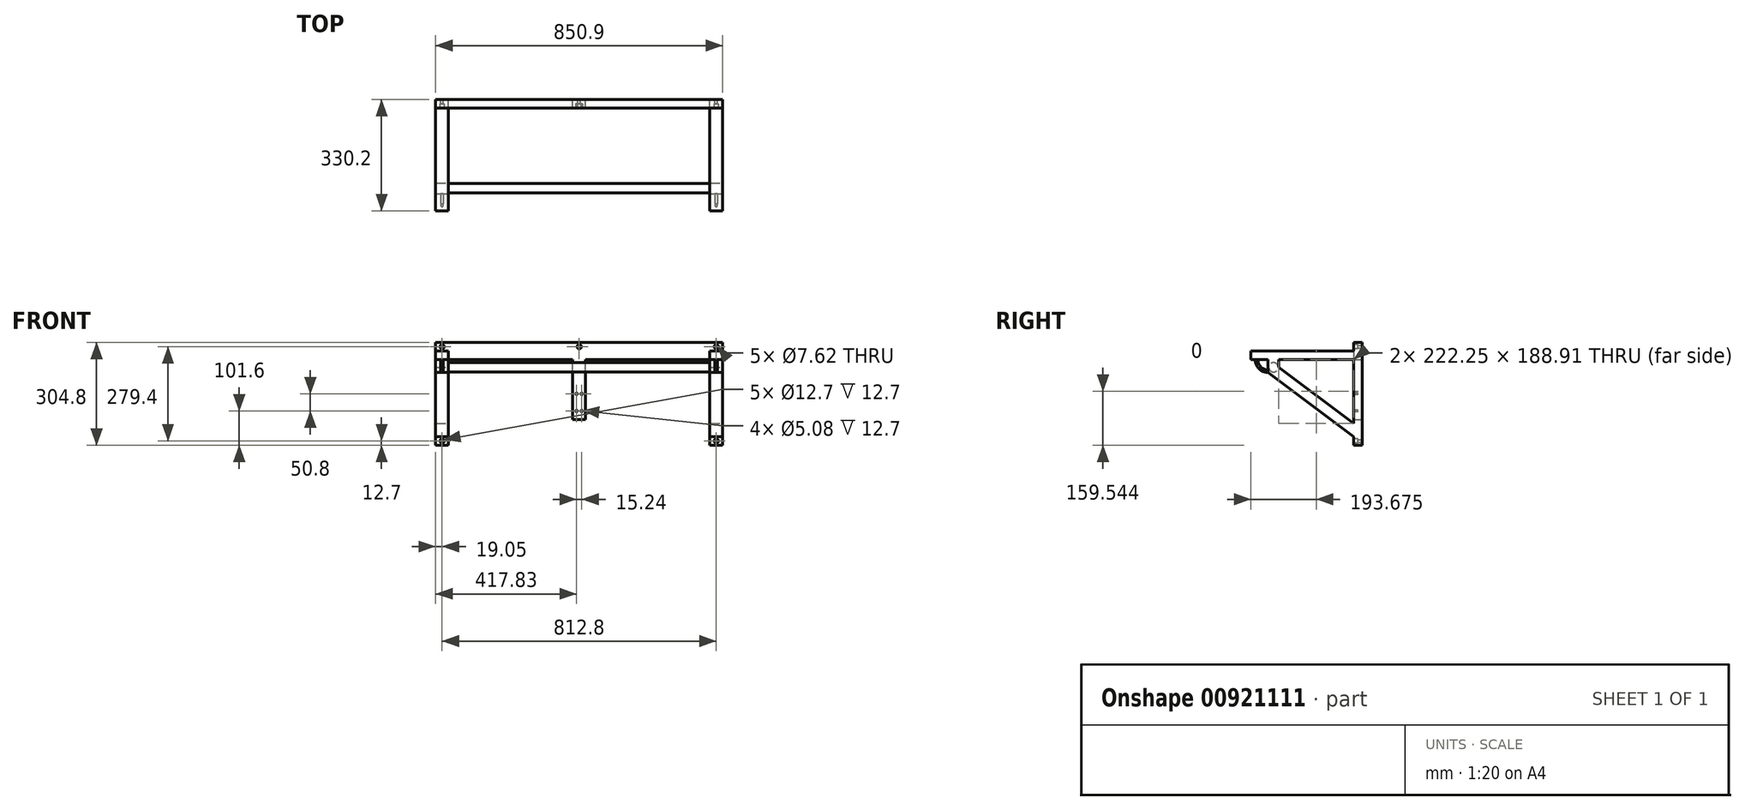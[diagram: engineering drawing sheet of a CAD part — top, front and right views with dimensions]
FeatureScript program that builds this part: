
annotation { "Feature Type Name" : "Feature", "Feature Type Description" : "" }
export const myFeature = defineFeature(function(context is Context, id is Id, definition is map)
    precondition{}
    {
        {
            var Q0;
            Q0=qCreatedBy(makeId("Front.planeOp"),FACE);
            var sketch = newSketch(context, id + "F0", { "sketchPlane" : qUnion([Q0])});
            skLineSegment(sketch, "E0.top", {"start": v(19.05, 152.4) * mm, "end": v(-19.05, 152.4) * mm});
            skLineSegment(sketch, "E0.left", {"start": v(19.05, -76.2) * mm, "end": v(19.05, 152.4) * mm});
            skLineSegment(sketch, "E0.right", {"start": v(-19.05, -76.2) * mm, "end": v(-19.05, 152.4) * mm});
            skPoint(sketch, "E0.middle", {"position": v(0, 0) * mm});
            skLineSegment(sketch, "E1.bottom", {"start": v(-387.35, -152.4) * mm, "end": v(-425.45, -152.4) * mm});
            skLineSegment(sketch, "E1.top", {"start": v(-387.35, 152.4) * mm, "end": v(-425.45, 152.4) * mm});
            skLineSegment(sketch, "E1.left", {"start": v(-387.35, -152.4) * mm, "end": v(-387.35, 152.4) * mm});
            skLineSegment(sketch, "E1.right", {"start": v(-425.45, -152.4) * mm, "end": v(-425.45, 152.4) * mm});
            skPoint(sketch, "E1.middle", {"position": v(-406.4, 0) * mm});
            skLineSegment(sketch, "E2.bottom", {"start": v(425.45, -152.4) * mm, "end": v(387.35, -152.4) * mm});
            skLineSegment(sketch, "E2.top", {"start": v(425.45, 152.4) * mm, "end": v(387.35, 152.4) * mm});
            skLineSegment(sketch, "E2.left", {"start": v(425.45, -152.4) * mm, "end": v(425.45, 152.4) * mm});
            skLineSegment(sketch, "E2.right", {"start": v(387.35, -152.4) * mm, "end": v(387.35, 152.4) * mm});
            skPoint(sketch, "E2.middle", {"position": v(406.4, 0) * mm});
            skLineSegment(sketch, "E3.bottom", {"start": v(425.45, 101.6) * mm, "end": v(-425.45, 101.6) * mm});
            skLineSegment(sketch, "E3.top", {"start": v(425.45, 127) * mm, "end": v(-425.45, 127) * mm});
            skLineSegment(sketch, "E3.left", {"start": v(425.45, 101.6) * mm, "end": v(425.45, 127) * mm});
            skLineSegment(sketch, "E3.right", {"start": v(-425.45, 101.6) * mm, "end": v(-425.45, 127) * mm});
            skPoint(sketch, "E3.middle", {"position": v(0, 114.3) * mm});
            skLineSegment(sketch, "E4", {"start": v(-19.05, -76.2) * mm, "end": v(19.05, -76.2) * mm});
            skPoint(sketch, "E0.bottom.end.orphan", {"position": v(-19.05, -152.4) * mm});
            skPoint(sketch, "E0.bottom.start.orphan", {"position": v(19.05, -152.4) * mm});
            skSolve(sketch);
        }
        {
            var Q0;
            Q0=qSketchRegion(id+"F0",true);
            extrude(context, id + "F1", {"entities" : qUnion([Q0]), "depth" : 25.4 * mm, "offsetDistance" : 25.4 * mm});
        }
        {
            var Q0;
            Q0=makeQuery(id+"F1.opExtrude","CAP_FACE",FACE,{"disambiguationData":[OSD([sQuery(id+"F0.wireOp",EDGE,"E0.bottom"),sQuery(id+"F0.wireOp",EDGE,"E0.top"),sQuery(id+"F0.wireOp",EDGE,"E0.left"),sQuery(id+"F0.wireOp",EDGE,"E0.right"),sQuery(id+"F0.wireOp",EDGE,"E1.bottom"),sQuery(id+"F0.wireOp",EDGE,"E1.top"),sQuery(id+"F0.wireOp",EDGE,"E1.left"),sQuery(id+"F0.wireOp",EDGE,"E1.right"),sQuery(id+"F0.wireOp",EDGE,"E2.bottom"),sQuery(id+"F0.wireOp",EDGE,"E2.top"),sQuery(id+"F0.wireOp",EDGE,"E2.left"),sQuery(id+"F0.wireOp",EDGE,"E2.right"),sQuery(id+"F0.wireOp",EDGE,"E3.bottom"),sQuery(id+"F0.wireOp",EDGE,"E3.top"),sQuery(id+"F0.wireOp",EDGE,"E3.left"),sQuery(id+"F0.wireOp",EDGE,"E3.right")])],"isStart":false});
            var sketch = newSketch(context, id + "F2", { "sketchPlane" : qUnion([Q0])});
            skLineSegment(sketch, "E5.bottom", {"start": v(-387.35, 101.6) * mm, "end": v(-425.45, 101.6) * mm});
            skLineSegment(sketch, "E5.top", {"start": v(-387.35, 127) * mm, "end": v(-425.45, 127) * mm});
            skLineSegment(sketch, "E5.left", {"start": v(-387.35, 101.6) * mm, "end": v(-387.35, 127) * mm});
            skLineSegment(sketch, "E5.right", {"start": v(-425.45, 101.6) * mm, "end": v(-425.45, 127) * mm});
            skLineSegment(sketch, "E6.bottom", {"start": v(387.35, 127) * mm, "end": v(425.45, 127) * mm});
            skLineSegment(sketch, "E6.top", {"start": v(387.35, 101.6) * mm, "end": v(425.45, 101.6) * mm});
            skLineSegment(sketch, "E6.left", {"start": v(387.35, 127) * mm, "end": v(387.35, 101.6) * mm});
            skLineSegment(sketch, "E6.right", {"start": v(425.45, 127) * mm, "end": v(425.45, 101.6) * mm});
            skSolve(sketch);
        }
        {
            var Q0;
            Q0=qSketchRegion(id+"F2",true);
            extrude(context, id + "F3", {"entities" : qUnion([Q0]), "operationType" : NewBodyOperationType.ADD, "depth" : 304.8 * mm, "offsetDistance" : 25.4 * mm});
        }
        {
            var Q0;
            {var subQ0=sQuery(id+"F0.wireOp",EDGE,"E1.left");var subQ1=sQuery(id+"F0.wireOp",EDGE,"E1.top");var subQ2=sQuery(id+"F0.wireOp",EDGE,"E3.top");var subQ4=sQuery(id+"F0.wireOp",EDGE,"E3.right");var subQ5=sQuery(id+"F0.wireOp",EDGE,"E1.right");var subQ6=sQuery(id+"F0.wireOp",EDGE,"E0.right");var subQ7=makeQuery(id+"F1.opExtrude","CAP_FACE",FACE,{"disambiguationData":[OSD([sQuery(id+"F0.wireOp",EDGE,"E0.bottom"),sQuery(id+"F0.wireOp",EDGE,"E0.top"),sQuery(id+"F0.wireOp",EDGE,"E0.left"),subQ6,sQuery(id+"F0.wireOp",EDGE,"E1.bottom"),subQ1,subQ0,subQ5,sQuery(id+"F0.wireOp",EDGE,"E2.bottom"),sQuery(id+"F0.wireOp",EDGE,"E2.top"),sQuery(id+"F0.wireOp",EDGE,"E2.left"),sQuery(id+"F0.wireOp",EDGE,"E2.right"),sQuery(id+"F0.wireOp",EDGE,"E3.bottom"),subQ2,sQuery(id+"F0.wireOp",EDGE,"E3.left"),subQ4])],"isStart":false});Q0=makeQuery(id+"F3.boolean.opBoolean","SPLIT",FACE,{"disambiguationData":[TD([subQ7,makeQuery(id+"F1.opExtrude","SWEPT_FACE",FACE,{"disambiguationData":[OSD([subQ1])]}),makeQuery(id+"F1.opExtrude","SWEPT_FACE",FACE,{"disambiguationData":[OSD([subQ0]),TDD([makeQuery(id+"F0.imprint","IMPRINT",EDGE,{"disambiguationData":[TD([[makeQuery(id+"F0.imprint","INTERSECT",VERTEX,{"derivedFrom":[subQ1,subQ0]}),1.0]])],"derivedFrom":subQ0})])]}),makeQuery(id+"F1.opExtrude","SWEPT_FACE",FACE,{"disambiguationData":[OSD([subQ5,subQ4])]}),makeQuery(id+"F1.opExtrude","SWEPT_FACE",FACE,{"disambiguationData":[OSD([subQ2]),TDD([makeQuery(id+"F0.imprint","IMPRINT",EDGE,{"disambiguationData":[TD([[makeQuery(id+"F0.imprint","INTERSECT",VERTEX,{"derivedFrom":[subQ6,subQ2]}),-1.0]])],"derivedFrom":subQ2})])]}),makeQuery(id+"F3.opExtrude","SWEPT_FACE",FACE,{"disambiguationData":[OSD([sQuery(id+"F2.wireOp",EDGE,"E5.top")])]}),makeQuery(id+"F3.opExtrude","SWEPT_FACE",FACE,{"disambiguationData":[OSD([sQuery(id+"F2.wireOp",EDGE,"E5.left")])]}),makeQuery(id+"F3.opExtrude","SWEPT_FACE",FACE,{"disambiguationData":[OSD([sQuery(id+"F2.wireOp",EDGE,"E5.right")])]})])],"derivedFrom":subQ7});}
            var sketch = newSketch(context, id + "F4", { "sketchPlane" : qUnion([Q0])});
            skLineSegment(sketch, "E7.bottom", {"start": v(-425.45, 152.4) * mm, "end": v(425.45, 152.4) * mm});
            skLineSegment(sketch, "E7.top", {"start": v(-425.45, 127) * mm, "end": v(425.45, 127) * mm});
            skLineSegment(sketch, "E7.left", {"start": v(-425.45, 152.4) * mm, "end": v(-425.45, 127) * mm});
            skLineSegment(sketch, "E7.right", {"start": v(425.45, 152.4) * mm, "end": v(425.45, 127) * mm});
            skSolve(sketch);
        }
        {
            var Q0;
            Q0=qSketchRegion(id+"F4",true);
            extrude(context, id + "F5", {"entities" : qUnion([Q0]), "operationType" : NewBodyOperationType.ADD, "oppositeDirection" : true, "depth" : 25.4 * mm, "offsetDistance" : 25.4 * mm});
        }
        {
            var Q0;
            Q0=makeQuery(id+"F3.boolean.opBoolean","MERGE",FACE,{"derivedFrom":[makeQuery(id+"F1.opExtrude","SWEPT_FACE",FACE,{"disambiguationData":[OSD([sQuery(id+"F0.wireOp",EDGE,"E2.left"),sQuery(id+"F0.wireOp",EDGE,"E3.left")])]}),makeQuery(id+"F3.opExtrude","SWEPT_FACE",FACE,{"disambiguationData":[OSD([sQuery(id+"F2.wireOp",EDGE,"E6.right")])]})]});
            var sketch = newSketch(context, id + "F6", { "sketchPlane" : qUnion([Q0])});
            skLineSegment(sketch, "E8", {"start": v(-25.4, -127) * mm, "end": v(-279.4, 63.5) * mm});
            skLineSegment(sketch, "E9", {"start": v(-279.4, 63.5) * mm, "end": v(-279.4, 101.6) * mm});
            skLineSegment(sketch, "E10", {"start": v(-279.4, 101.6) * mm, "end": v(-247.65, 101.6) * mm});
            skLineSegment(sketch, "E11", {"start": v(-247.65, 101.6) * mm, "end": v(-247.65, 79.38) * mm});
            skLineSegment(sketch, "E12", {"start": v(-247.65, 79.38) * mm, "end": v(-25.4, -87.31) * mm});
            skLineSegment(sketch, "E13", {"start": v(-25.4, -87.31) * mm, "end": v(-25.4, -127) * mm});
            skSolve(sketch);
        }
        {
            var Q0;
            Q0=qSketchRegion(id+"F6",true);
            extrude(context, id + "F7", {"entities" : qUnion([Q0]), "operationType" : NewBodyOperationType.ADD, "oppositeDirection" : true, "depth" : 38.1 * mm, "offsetDistance" : 25.4 * mm});
        }
        {
            var Q0;
            Q0=makeQuery(id+"F3.opExtrude","SWEPT_FACE",FACE,{"disambiguationData":[OSD([sQuery(id+"F2.wireOp",EDGE,"E5.left")])]});
            var sketch = newSketch(context, id + "F8", { "sketchPlane" : qUnion([Q0])});
            skLineSegment(sketch, "E14", {"start": v(-25.4, -127) * mm, "end": v(-279.4, 63.5) * mm});
            skLineSegment(sketch, "E15", {"start": v(-279.4, 63.5) * mm, "end": v(-279.4, 101.6) * mm});
            skLineSegment(sketch, "E16", {"start": v(-279.4, 101.6) * mm, "end": v(-247.65, 101.6) * mm});
            skLineSegment(sketch, "E17", {"start": v(-247.65, 101.6) * mm, "end": v(-247.65, 79.38) * mm});
            skLineSegment(sketch, "E18", {"start": v(-247.65, 79.38) * mm, "end": v(-25.4, -87.31) * mm});
            skLineSegment(sketch, "E19", {"start": v(-25.4, -87.31) * mm, "end": v(-25.4, -127) * mm});
            skSolve(sketch);
        }
        {
            var Q0;
            Q0=qSketchRegion(id+"F8",true);
            extrude(context, id + "F9", {"entities" : qUnion([Q0]), "operationType" : NewBodyOperationType.ADD, "oppositeDirection" : true, "depth" : 38.1 * mm, "offsetDistance" : 25.4 * mm});
        }
        {
            var Q0;
            {var subQ0=sQuery(id+"F0.wireOp",EDGE,"E0.right");var subQ1=sQuery(id+"F0.wireOp",EDGE,"E0.bottom");var subQ2=sQuery(id+"F0.wireOp",EDGE,"E3.bottom");var subQ3=makeQuery(id+"F0.imprint","INTERSECT",VERTEX,{"derivedFrom":[subQ0,subQ2]});var subQ4=sQuery(id+"F0.wireOp",EDGE,"E0.left");var subQ5=makeQuery(id+"F0.imprint","INTERSECT",VERTEX,{"derivedFrom":[subQ4,subQ2]});var subQ6=sQuery(id+"F0.wireOp",EDGE,"E2.right");var subQ7=sQuery(id+"F0.wireOp",EDGE,"E1.left");var subQ8=makeQuery(id+"F1.opExtrude","CAP_FACE",FACE,{"disambiguationData":[OSD([subQ1,sQuery(id+"F0.wireOp",EDGE,"E0.top"),subQ4,subQ0,sQuery(id+"F0.wireOp",EDGE,"E1.bottom"),sQuery(id+"F0.wireOp",EDGE,"E1.top"),subQ7,sQuery(id+"F0.wireOp",EDGE,"E1.right"),sQuery(id+"F0.wireOp",EDGE,"E2.bottom"),sQuery(id+"F0.wireOp",EDGE,"E2.top"),sQuery(id+"F0.wireOp",EDGE,"E2.left"),subQ6,subQ2,sQuery(id+"F0.wireOp",EDGE,"E3.top"),sQuery(id+"F0.wireOp",EDGE,"E3.left"),sQuery(id+"F0.wireOp",EDGE,"E3.right")])],"isStart":false});Q0=makeQuery(id+"F3.boolean.opBoolean","SPLIT",FACE,{"disambiguationData":[TD([makeQuery(id+"F1.opExtrude","SWEPT_FACE",FACE,{"disambiguationData":[OSD([subQ1])]}),subQ8,makeQuery(id+"F1.opExtrude","SWEPT_FACE",FACE,{"disambiguationData":[OSD([subQ4]),TDD([makeQuery(id+"F0.imprint","IMPRINT",EDGE,{"disambiguationData":[TD([[makeQuery(id+"F0.imprint","INTERSECT",VERTEX,{"derivedFrom":[subQ1,subQ4]}),-1.0]])],"derivedFrom":subQ4})])]}),makeQuery(id+"F1.opExtrude","SWEPT_FACE",FACE,{"disambiguationData":[OSD([subQ0]),TDD([makeQuery(id+"F0.imprint","IMPRINT",EDGE,{"disambiguationData":[TD([[makeQuery(id+"F0.imprint","INTERSECT",VERTEX,{"derivedFrom":[subQ1,subQ0]}),-1.0]])],"derivedFrom":subQ0})])]}),makeQuery(id+"F1.opExtrude","SWEPT_FACE",FACE,{"disambiguationData":[OSD([subQ2]),TDD([makeQuery(id+"F0.imprint","IMPRINT",EDGE,{"disambiguationData":[TD([[subQ5,1.0]])],"derivedFrom":subQ2})])]}),makeQuery(id+"F1.opExtrude","SWEPT_FACE",FACE,{"disambiguationData":[OSD([subQ2]),TDD([makeQuery(id+"F0.imprint","IMPRINT",EDGE,{"disambiguationData":[TD([[subQ3,-1.0]])],"derivedFrom":subQ2})])]}),makeQuery(id+"F3.opExtrude","SWEPT_FACE",FACE,{"disambiguationData":[OSD([sQuery(id+"F2.wireOp",EDGE,"KpovKg3x-hCtO-uOXG-gug3-TiywYrCm03ZB.top")])]}),makeQuery(id+"F3.opExtrude","SWEPT_FACE",FACE,{"disambiguationData":[OSD([sQuery(id+"F2.wireOp",EDGE,"KpovKg3x-hCtO-uOXG-gug3-TiywYrCm03ZB.left")])]}),makeQuery(id+"F3.opExtrude","SWEPT_FACE",FACE,{"disambiguationData":[OSD([sQuery(id+"F2.wireOp",EDGE,"KpovKg3x-hCtO-uOXG-gug3-TiywYrCm03ZB.right")])]})])],"derivedFrom":subQ8});}
            var sketch = newSketch(context, id + "F10", { "sketchPlane" : qUnion([Q0])});
            skCircle(sketch, "E20", {"center": v(-7.62, 0) * mm, "radius": 2.54 * mm});
            skCircle(sketch, "E21.MirrorC", {"center": v(7.62, 0) * mm, "radius": 2.54 * mm});
            skCircle(sketch, "E22.MirrorC", {"center": v(-7.62, -50.8) * mm, "radius": 2.54 * mm});
            skCircle(sketch, "E23.MirrorC", {"center": v(7.62, -50.8) * mm, "radius": 2.54 * mm});
            skSolve(sketch);
        }
        {
            var Q0;
            Q0=qSketchRegion(id+"F10",true);
            extrude(context, id + "F11", {"entities" : qUnion([Q0]), "operationType" : NewBodyOperationType.REMOVE, "oppositeDirection" : true, "depth" : 12.7 * mm, "offsetDistance" : 25.4 * mm});
        }
        {
            var Q0;
            Q0=qCreatedBy(makeId("Right.planeOp"),FACE);
            var sketch = newSketch(context, id + "F12", { "sketchPlane" : qUnion([Q0])});
            skCircle(sketch, "E24", {"center": v(-263.27, 78.74) * mm, "radius": 13.97 * mm});
            skSolve(sketch);
        }
        {
            var Q0;
            Q0=qSketchRegion(id+"F12",true);
            extrude(context, id + "F13", {"entities" : qUnion([Q0]), "operationType" : NewBodyOperationType.ADD, "oppositeDirection" : true, "depth" : 406.4 * mm, "offsetDistance" : 25.4 * mm, "hasSecondDirection" : true, "secondDirectionOppositeDirection" : false, "secondDirectionDepth" : 406.4 * mm});
        }
        {
            var Q0;
            Q0=makeQuery(id+"F9.boolean.opBoolean","MERGE",FACE,{"derivedFrom":[makeQuery(id+"F3.boolean.opBoolean","MERGE",FACE,{"derivedFrom":[makeQuery(id+"F1.opExtrude","SWEPT_FACE",FACE,{"disambiguationData":[OSD([sQuery(id+"F0.wireOp",EDGE,"E1.right"),sQuery(id+"F0.wireOp",EDGE,"E3.right")])]}),makeQuery(id+"F3.opExtrude","SWEPT_FACE",FACE,{"disambiguationData":[OSD([sQuery(id+"F2.wireOp",EDGE,"E5.right")])]})]}),makeQuery(id+"F9.opExtrude","CAP_FACE",FACE,{"disambiguationData":[OSD([sQuery(id+"F8.wireOp",EDGE,"E14"),sQuery(id+"F8.wireOp",EDGE,"E15"),sQuery(id+"F8.wireOp",EDGE,"E16"),sQuery(id+"F8.wireOp",EDGE,"E17"),sQuery(id+"F8.wireOp",EDGE,"E18"),sQuery(id+"F8.wireOp",EDGE,"E19")])],"isStart":false})]});
            var sketch = newSketch(context, id + "F14", { "sketchPlane" : qUnion([Q0])});
            skArc(sketch, "E25", {"start": v(279.4, 63.5) * mm, "mid": v(306.34, 74.66) * mm, "end": v(317.5, 101.6) * mm});
            skArc(sketch, "E26", {"start": v(279.4, 71.12) * mm, "mid": v(300.95, 80.05) * mm, "end": v(309.88, 101.6) * mm});
            skLineSegment(sketch, "E27", {"start": v(309.88, 101.6) * mm, "end": v(317.5, 101.6) * mm});
            skLineSegment(sketch, "E28", {"start": v(279.4, 63.5) * mm, "end": v(279.4, 71.12) * mm});
            skSolve(sketch);
        }
        {
            var Q0;
            Q0=qSketchRegion(id+"F14",true);
            extrude(context, id + "F15", {"entities" : qUnion([Q0]), "operationType" : NewBodyOperationType.ADD, "oppositeDirection" : true, "depth" : 38.1 * mm, "offsetDistance" : 25.4 * mm});
        }
        {
            var Q0;
            {var subQ0=sQuery(id+"F0.wireOp",EDGE,"E2.right");Q0=makeQuery(id+"F7.boolean.opBoolean","MERGE",FACE,{"derivedFrom":[makeQuery(id+"F1.opExtrude","SWEPT_FACE",FACE,{"disambiguationData":[OSD([subQ0]),TDD([makeQuery(id+"F0.imprint","IMPRINT",EDGE,{"disambiguationData":[TD([[makeQuery(id+"F0.imprint","INTERSECT",VERTEX,{"derivedFrom":[sQuery(id+"F0.wireOp",EDGE,"E2.bottom"),subQ0]}),-1.0]])],"derivedFrom":subQ0})])]}),makeQuery(id+"F3.opExtrude","SWEPT_FACE",FACE,{"disambiguationData":[OSD([sQuery(id+"F2.wireOp",EDGE,"E6.left")])]}),makeQuery(id+"F7.opExtrude","CAP_FACE",FACE,{"disambiguationData":[OSD([sQuery(id+"F6.wireOp",EDGE,"E8"),sQuery(id+"F6.wireOp",EDGE,"E9"),sQuery(id+"F6.wireOp",EDGE,"E10"),sQuery(id+"F6.wireOp",EDGE,"E11"),sQuery(id+"F6.wireOp",EDGE,"E12"),sQuery(id+"F6.wireOp",EDGE,"E13")])],"isStart":false})]});}
            var sketch = newSketch(context, id + "F16", { "sketchPlane" : qUnion([Q0])});
            skArc(sketch, "E29", {"start": v(279.4, 63.5) * mm, "mid": v(306.34, 74.66) * mm, "end": v(317.5, 101.6) * mm});
            skArc(sketch, "E30", {"start": v(279.4, 71.12) * mm, "mid": v(300.95, 80.05) * mm, "end": v(309.88, 101.6) * mm});
            skLineSegment(sketch, "E31", {"start": v(309.88, 101.6) * mm, "end": v(317.5, 101.6) * mm});
            skLineSegment(sketch, "E32", {"start": v(279.4, 63.5) * mm, "end": v(279.4, 71.12) * mm});
            skSolve(sketch);
        }
        {
            var Q0;
            Q0=qSketchRegion(id+"F16",true);
            extrude(context, id + "F17", {"entities" : qUnion([Q0]), "operationType" : NewBodyOperationType.ADD, "oppositeDirection" : true, "depth" : 38.1 * mm, "offsetDistance" : 25.4 * mm});
        }
        {
            var Q0;
            Q0=makeQuery(id+"F3.opExtrude","CAP_FACE",FACE,{"disambiguationData":[OSD([sQuery(id+"F2.wireOp",EDGE,"E5.bottom"),sQuery(id+"F2.wireOp",EDGE,"E5.top"),sQuery(id+"F2.wireOp",EDGE,"E5.left"),sQuery(id+"F2.wireOp",EDGE,"E5.right")])],"isStart":false});
            var sketch = newSketch(context, id + "F18", { "sketchPlane" : qUnion([Q0])});
            skLineSegment(sketch, "E33.bottom", {"start": v(-425.45, 101.6) * mm, "end": v(-410.21, 101.6) * mm});
            skLineSegment(sketch, "E33.top", {"start": v(-425.45, 62.58) * mm, "end": v(-410.21, 62.58) * mm});
            skLineSegment(sketch, "E33.left", {"start": v(-425.45, 101.6) * mm, "end": v(-425.45, 62.58) * mm});
            skLineSegment(sketch, "E33.right", {"start": v(-410.21, 101.6) * mm, "end": v(-410.21, 62.58) * mm});
            skLineSegment(sketch, "E34.bottom", {"start": v(-387.35, 101.6) * mm, "end": v(-402.59, 101.6) * mm});
            skLineSegment(sketch, "E34.top", {"start": v(-387.35, 62.58) * mm, "end": v(-402.59, 62.58) * mm});
            skLineSegment(sketch, "E34.left", {"start": v(-387.35, 101.6) * mm, "end": v(-387.35, 62.58) * mm});
            skLineSegment(sketch, "E34.right", {"start": v(-402.59, 101.6) * mm, "end": v(-402.59, 62.58) * mm});
            skSolve(sketch);
        }
        {
            var Q0;
            Q0=qSketchRegion(id+"F18",true);
            extrude(context, id + "F19", {"entities" : qUnion([Q0]), "operationType" : NewBodyOperationType.REMOVE, "oppositeDirection" : true, "depth" : 50.8 * mm, "offsetDistance" : 25.4 * mm});
        }
        {
            var Q0;
            Q0=makeQuery(id+"F3.opExtrude","CAP_FACE",FACE,{"disambiguationData":[OSD([sQuery(id+"F2.wireOp",EDGE,"E6.bottom"),sQuery(id+"F2.wireOp",EDGE,"E6.top"),sQuery(id+"F2.wireOp",EDGE,"E6.left"),sQuery(id+"F2.wireOp",EDGE,"E6.right")])],"isStart":false});
            var sketch = newSketch(context, id + "F20", { "sketchPlane" : qUnion([Q0])});
            skLineSegment(sketch, "E35.bottom", {"start": v(387.35, 101.6) * mm, "end": v(402.59, 101.6) * mm});
            skLineSegment(sketch, "E35.top", {"start": v(387.35, 62.58) * mm, "end": v(402.59, 62.58) * mm});
            skLineSegment(sketch, "E35.left", {"start": v(387.35, 101.6) * mm, "end": v(387.35, 62.58) * mm});
            skLineSegment(sketch, "E35.right", {"start": v(402.59, 101.6) * mm, "end": v(402.59, 62.58) * mm});
            skLineSegment(sketch, "E36.bottom", {"start": v(425.45, 101.6) * mm, "end": v(410.21, 101.6) * mm});
            skLineSegment(sketch, "E36.top", {"start": v(425.45, 62.58) * mm, "end": v(410.21, 62.58) * mm});
            skLineSegment(sketch, "E36.left", {"start": v(425.45, 101.6) * mm, "end": v(425.45, 62.58) * mm});
            skLineSegment(sketch, "E36.right", {"start": v(410.21, 101.6) * mm, "end": v(410.21, 62.58) * mm});
            skSolve(sketch);
        }
        {
            var Q0;
            Q0=qSketchRegion(id+"F20",true);
            extrude(context, id + "F21", {"entities" : qUnion([Q0]), "operationType" : NewBodyOperationType.REMOVE, "oppositeDirection" : true, "depth" : 50.8 * mm, "offsetDistance" : 25.4 * mm});
        }
        {
            var Q0;
            Q0=makeQuery(id+"F21.boolean.opBoolean","INTERSECT",EDGE,{"derivedFrom":[makeQuery(id+"F17.opExtrude","SWEPT_FACE",FACE,{"disambiguationData":[OSD([sQuery(id+"F16.wireOp",EDGE,"E29")])]}),makeQuery(id+"F21.opExtrude","SWEPT_FACE",FACE,{"disambiguationData":[OSD([sQuery(id+"F20.wireOp",EDGE,"E35.right")])]})]});
            var Q1;
            Q1=makeQuery(id+"F21.boolean.opBoolean","INTERSECT",EDGE,{"derivedFrom":[makeQuery(id+"F17.opExtrude","SWEPT_FACE",FACE,{"disambiguationData":[OSD([sQuery(id+"F16.wireOp",EDGE,"E30")])]}),makeQuery(id+"F21.opExtrude","SWEPT_FACE",FACE,{"disambiguationData":[OSD([sQuery(id+"F20.wireOp",EDGE,"E35.right")])]})]});
            var Q2;
            Q2=makeQuery(id+"F21.boolean.opBoolean","INTERSECT",EDGE,{"derivedFrom":[makeQuery(id+"F17.opExtrude","SWEPT_FACE",FACE,{"disambiguationData":[OSD([sQuery(id+"F16.wireOp",EDGE,"E29")])]}),makeQuery(id+"F21.opExtrude","SWEPT_FACE",FACE,{"disambiguationData":[OSD([sQuery(id+"F20.wireOp",EDGE,"E36.right")])]})]});
            var Q3;
            Q3=makeQuery(id+"F21.boolean.opBoolean","INTERSECT",EDGE,{"derivedFrom":[makeQuery(id+"F17.opExtrude","SWEPT_FACE",FACE,{"disambiguationData":[OSD([sQuery(id+"F16.wireOp",EDGE,"E30")])]}),makeQuery(id+"F21.opExtrude","SWEPT_FACE",FACE,{"disambiguationData":[OSD([sQuery(id+"F20.wireOp",EDGE,"E36.right")])]})]});
            var Q4;
            Q4=makeQuery(id+"FiMfmLP1IDfUJ7z_1.boolean.opBoolean","INTERSECT",EDGE,{"derivedFrom":[makeQuery(id+"FR193NCc5tIVFVq_1.opExtrude","SWEPT_FACE",FACE,{"disambiguationData":[OSD([sQuery(id+"FKuXT1YgNFIZP2d.wireOp",EDGE,"3eea3fe8-574d-4fa1-90f3-3fdec882c41a")])]}),makeQuery(id+"FiMfmLP1IDfUJ7z_1.opExtrude","SWEPT_FACE",FACE,{"disambiguationData":[OSD([sQuery(id+"F6qNrr9CfzusgMp.wireOp",EDGE,"3619d014-cc36-4aa5-92e5-1d4587400a18.right")])]})]});
            var Q5;
            Q5=makeQuery(id+"FiMfmLP1IDfUJ7z_1.boolean.opBoolean","INTERSECT",EDGE,{"derivedFrom":[makeQuery(id+"FR193NCc5tIVFVq_1.opExtrude","SWEPT_FACE",FACE,{"disambiguationData":[OSD([sQuery(id+"FKuXT1YgNFIZP2d.wireOp",EDGE,"f7dacc9f-6ae9-4327-9814-fc3a381e29a1")])]}),makeQuery(id+"FiMfmLP1IDfUJ7z_1.opExtrude","SWEPT_FACE",FACE,{"disambiguationData":[OSD([sQuery(id+"F6qNrr9CfzusgMp.wireOp",EDGE,"3619d014-cc36-4aa5-92e5-1d4587400a18.right")])]})]});
            var Q6;
            Q6=makeQuery(id+"FiMfmLP1IDfUJ7z_1.boolean.opBoolean","INTERSECT",EDGE,{"derivedFrom":[makeQuery(id+"FR193NCc5tIVFVq_1.opExtrude","SWEPT_FACE",FACE,{"disambiguationData":[OSD([sQuery(id+"FKuXT1YgNFIZP2d.wireOp",EDGE,"3eea3fe8-574d-4fa1-90f3-3fdec882c41a")])]}),makeQuery(id+"FiMfmLP1IDfUJ7z_1.opExtrude","SWEPT_FACE",FACE,{"disambiguationData":[OSD([sQuery(id+"F6qNrr9CfzusgMp.wireOp",EDGE,"b5c9d8e0-27cf-4a16-8ede-d885acafefaf.right")])]})]});
            var Q7;
            Q7=makeQuery(id+"FiMfmLP1IDfUJ7z_1.boolean.opBoolean","INTERSECT",EDGE,{"derivedFrom":[makeQuery(id+"FR193NCc5tIVFVq_1.opExtrude","SWEPT_FACE",FACE,{"disambiguationData":[OSD([sQuery(id+"FKuXT1YgNFIZP2d.wireOp",EDGE,"f7dacc9f-6ae9-4327-9814-fc3a381e29a1")])]}),makeQuery(id+"FiMfmLP1IDfUJ7z_1.opExtrude","SWEPT_FACE",FACE,{"disambiguationData":[OSD([sQuery(id+"F6qNrr9CfzusgMp.wireOp",EDGE,"b5c9d8e0-27cf-4a16-8ede-d885acafefaf.right")])]})]});
            var Q8;
            Q8=makeQuery(id+"F19.boolean.opBoolean","INTERSECT",EDGE,{"derivedFrom":[makeQuery(id+"F15.opExtrude","SWEPT_FACE",FACE,{"disambiguationData":[OSD([sQuery(id+"F14.wireOp",EDGE,"E26")])]}),makeQuery(id+"F19.opExtrude","SWEPT_FACE",FACE,{"disambiguationData":[OSD([sQuery(id+"F18.wireOp",EDGE,"E33.right")])]})]});
            var Q9;
            Q9=makeQuery(id+"F19.boolean.opBoolean","INTERSECT",EDGE,{"derivedFrom":[makeQuery(id+"F15.opExtrude","SWEPT_FACE",FACE,{"disambiguationData":[OSD([sQuery(id+"F14.wireOp",EDGE,"E25")])]}),makeQuery(id+"F19.opExtrude","SWEPT_FACE",FACE,{"disambiguationData":[OSD([sQuery(id+"F18.wireOp",EDGE,"E33.right")])]})]});
            var Q10;
            Q10=makeQuery(id+"F19.boolean.opBoolean","INTERSECT",EDGE,{"derivedFrom":[makeQuery(id+"F15.opExtrude","SWEPT_FACE",FACE,{"disambiguationData":[OSD([sQuery(id+"F14.wireOp",EDGE,"E26")])]}),makeQuery(id+"F19.opExtrude","SWEPT_FACE",FACE,{"disambiguationData":[OSD([sQuery(id+"F18.wireOp",EDGE,"E34.right")])]})]});
            var Q11;
            Q11=makeQuery(id+"F19.boolean.opBoolean","INTERSECT",EDGE,{"derivedFrom":[makeQuery(id+"F15.opExtrude","SWEPT_FACE",FACE,{"disambiguationData":[OSD([sQuery(id+"F14.wireOp",EDGE,"E25")])]}),makeQuery(id+"F19.opExtrude","SWEPT_FACE",FACE,{"disambiguationData":[OSD([sQuery(id+"F18.wireOp",EDGE,"E34.right")])]})]});
            fillet(context, id + "F22", {"entities" : qUnion([Q0, Q1, Q2, Q3, Q4, Q5, Q6, Q7, Q8, Q9, Q10, Q11]), "radius" : 3.8 * mm, "tangentPropagation" : true, "allowEdgeOverflow" : false});
        }
        {
            var Q0;
            Q0=makeQuery(id+"F5.boolean.opBoolean","MERGE",FACE,{"derivedFrom":[makeQuery(id+"F1.opExtrude","CAP_FACE",FACE,{"disambiguationData":[OSD([sQuery(id+"F0.wireOp",EDGE,"E0.bottom"),sQuery(id+"F0.wireOp",EDGE,"E0.top"),sQuery(id+"F0.wireOp",EDGE,"E0.left"),sQuery(id+"F0.wireOp",EDGE,"E0.right"),sQuery(id+"F0.wireOp",EDGE,"E1.bottom"),sQuery(id+"F0.wireOp",EDGE,"E1.top"),sQuery(id+"F0.wireOp",EDGE,"E1.left"),sQuery(id+"F0.wireOp",EDGE,"E1.right"),sQuery(id+"F0.wireOp",EDGE,"E2.bottom"),sQuery(id+"F0.wireOp",EDGE,"E2.top"),sQuery(id+"F0.wireOp",EDGE,"E2.left"),sQuery(id+"F0.wireOp",EDGE,"E2.right"),sQuery(id+"F0.wireOp",EDGE,"E3.bottom"),sQuery(id+"F0.wireOp",EDGE,"E3.top"),sQuery(id+"F0.wireOp",EDGE,"E3.left"),sQuery(id+"F0.wireOp",EDGE,"E3.right")])],"isStart":true}),makeQuery(id+"F5.opExtrude","CAP_FACE",FACE,{"disambiguationData":[OSD([sQuery(id+"F4.wireOp",EDGE,"E7.bottom"),sQuery(id+"F4.wireOp",EDGE,"E7.top"),sQuery(id+"F4.wireOp",EDGE,"E7.left"),sQuery(id+"F4.wireOp",EDGE,"E7.right")])],"isStart":false})]});
            var sketch = newSketch(context, id + "F23", { "sketchPlane" : qUnion([Q0])});
            skCircle(sketch, "E37", {"center": v(0, 139.7) * mm, "radius": 3.81 * mm});
            skCircle(sketch, "E38", {"center": v(-406.4, 139.7) * mm, "radius": 3.81 * mm});
            skPoint(sketch, "E38.centerSnap0", {"position": v(-406.4, -152.4) * mm});
            skCircle(sketch, "E39", {"center": v(-406.4, -139.7) * mm, "radius": 3.81 * mm});
            skCircle(sketch, "E40", {"center": v(406.4, -139.7) * mm, "radius": 3.81 * mm});
            skPoint(sketch, "E40.centerSnap0", {"position": v(406.4, -152.4) * mm});
            skCircle(sketch, "E41", {"center": v(406.4, 139.7) * mm, "radius": 3.81 * mm});
            skSolve(sketch);
        }
        {
            var Q0;
            Q0=qSketchRegion(id+"F23",true);
            extrude(context, id + "F24", {"entities" : qUnion([Q0]), "operationType" : NewBodyOperationType.REMOVE, "oppositeDirection" : true, "depth" : 25.4 * mm, "offsetDistance" : 25.4 * mm});
        }
        {
            var Q0;
            {var subQ0=sQuery(id+"F0.wireOp",EDGE,"E3.left");var subQ1=sQuery(id+"F0.wireOp",EDGE,"E2.left");var subQ2=sQuery(id+"F0.wireOp",EDGE,"E2.top");var subQ3=sQuery(id+"F0.wireOp",EDGE,"E2.right");var subQ4=sQuery(id+"F0.wireOp",EDGE,"E3.top");var subQ6=makeQuery(id+"F1.opExtrude","SWEPT_FACE",FACE,{"disambiguationData":[OSD([subQ3]),TDD([makeQuery(id+"F0.imprint","IMPRINT",EDGE,{"disambiguationData":[TD([[makeQuery(id+"F0.imprint","INTERSECT",VERTEX,{"derivedFrom":[subQ2,subQ3]}),1.0]])],"derivedFrom":subQ3})])]});var subQ7=makeQuery(id+"F3.opExtrude","SWEPT_FACE",FACE,{"disambiguationData":[OSD([sQuery(id+"F2.wireOp",EDGE,"E6.left")])]});var subQ8=sQuery(id+"F0.wireOp",EDGE,"E3.right");var subQ9=sQuery(id+"F0.wireOp",EDGE,"E3.bottom");var subQ10=sQuery(id+"F0.wireOp",EDGE,"E2.bottom");var subQ11=sQuery(id+"F0.wireOp",EDGE,"E1.right");var subQ12=sQuery(id+"F0.wireOp",EDGE,"E1.left");var subQ13=sQuery(id+"F0.wireOp",EDGE,"E1.top");var subQ14=sQuery(id+"F0.wireOp",EDGE,"E1.bottom");var subQ15=sQuery(id+"F0.wireOp",EDGE,"E0.right");var subQ16=sQuery(id+"F0.wireOp",EDGE,"E0.left");var subQ17=sQuery(id+"F0.wireOp",EDGE,"E0.top");var subQ18=sQuery(id+"F0.wireOp",EDGE,"E0.bottom");var subQ19=makeQuery(id+"F1.opExtrude","CAP_FACE",FACE,{"disambiguationData":[OSD([subQ18,subQ17,subQ16,subQ15,subQ14,subQ13,subQ12,subQ11,subQ10,subQ2,subQ1,subQ3,subQ9,subQ4,subQ0,subQ8])],"isStart":false});var subQ20=makeQuery(id+"F3.opExtrude","SWEPT_FACE",FACE,{"disambiguationData":[OSD([sQuery(id+"F2.wireOp",EDGE,"E6.bottom")])]});var subQ21=makeQuery(id+"F0.imprint","INTERSECT",VERTEX,{"derivedFrom":[subQ16,subQ4]});var subQ22=makeQuery(id+"F1.opExtrude","SWEPT_FACE",FACE,{"disambiguationData":[OSD([subQ4]),TDD([makeQuery(id+"F0.imprint","IMPRINT",EDGE,{"disambiguationData":[TD([[subQ21,1.0]])],"derivedFrom":subQ4})])]});var subQ24=makeQuery(id+"F1.opExtrude","SWEPT_FACE",FACE,{"disambiguationData":[OSD([subQ12]),TDD([makeQuery(id+"F0.imprint","IMPRINT",EDGE,{"disambiguationData":[TD([[makeQuery(id+"F0.imprint","INTERSECT",VERTEX,{"derivedFrom":[subQ13,subQ12]}),1.0]])],"derivedFrom":subQ12})])]});var subQ25=makeQuery(id+"F0.imprint","INTERSECT",VERTEX,{"derivedFrom":[subQ15,subQ4]});var subQ26=makeQuery(id+"F1.opExtrude","SWEPT_FACE",FACE,{"disambiguationData":[OSD([subQ4]),TDD([makeQuery(id+"F0.imprint","IMPRINT",EDGE,{"disambiguationData":[TD([[subQ25,-1.0]])],"derivedFrom":subQ4})])]});var subQ27=makeQuery(id+"F3.opExtrude","SWEPT_FACE",FACE,{"disambiguationData":[OSD([sQuery(id+"F2.wireOp",EDGE,"E5.top")])]});var subQ28=makeQuery(id+"F3.opExtrude","SWEPT_FACE",FACE,{"disambiguationData":[OSD([sQuery(id+"F2.wireOp",EDGE,"E5.left")])]});var subQ29=makeQuery(id+"F1.opExtrude","SWEPT_FACE",FACE,{"disambiguationData":[OSD([subQ15]),TDD([makeQuery(id+"F0.imprint","IMPRINT",EDGE,{"disambiguationData":[TD([[makeQuery(id+"F0.imprint","INTERSECT",VERTEX,{"derivedFrom":[subQ17,subQ15]}),1.0]])],"derivedFrom":subQ15})])]});var subQ30=makeQuery(id+"F0.imprint","INTERSECT",VERTEX,{"derivedFrom":[subQ15,subQ9]});var subQ32=makeQuery(id+"F3.opExtrude","SWEPT_FACE",FACE,{"disambiguationData":[OSD([sQuery(id+"F2.wireOp",EDGE,"KpovKg3x-hCtO-uOXG-gug3-TiywYrCm03ZB.bottom")])]});var subQ33=makeQuery(id+"F3.opExtrude","SWEPT_FACE",FACE,{"disambiguationData":[OSD([sQuery(id+"F2.wireOp",EDGE,"KpovKg3x-hCtO-uOXG-gug3-TiywYrCm03ZB.top")])]});var subQ34=makeQuery(id+"F3.opExtrude","SWEPT_FACE",FACE,{"disambiguationData":[OSD([sQuery(id+"F2.wireOp",EDGE,"KpovKg3x-hCtO-uOXG-gug3-TiywYrCm03ZB.left")])]});var subQ35=makeQuery(id+"F3.opExtrude","SWEPT_FACE",FACE,{"disambiguationData":[OSD([sQuery(id+"F2.wireOp",EDGE,"KpovKg3x-hCtO-uOXG-gug3-TiywYrCm03ZB.right")])]});var subQ36=makeQuery(id+"F0.imprint","INTERSECT",VERTEX,{"derivedFrom":[subQ16,subQ9]});var subQ38=makeQuery(id+"F1.opExtrude","SWEPT_FACE",FACE,{"disambiguationData":[OSD([subQ16]),TDD([makeQuery(id+"F0.imprint","IMPRINT",EDGE,{"disambiguationData":[TD([[makeQuery(id+"F0.imprint","INTERSECT",VERTEX,{"derivedFrom":[subQ17,subQ16]}),1.0]])],"derivedFrom":subQ16})])]});Q0=makeQuery(id+"F5.boolean.opBoolean","MERGE",FACE,{"derivedFrom":[makeQuery(id+"F3.boolean.opBoolean","SPLIT",FACE,{"disambiguationData":[TD([subQ19,makeQuery(id+"F1.opExtrude","SWEPT_FACE",FACE,{"disambiguationData":[OSD([subQ17])]}),subQ38,subQ29,subQ22,subQ26,subQ32,subQ34,subQ35])],"derivedFrom":subQ19}),makeQuery(id+"F3.boolean.opBoolean","SPLIT",FACE,{"disambiguationData":[TD([subQ19,makeQuery(id+"F1.opExtrude","SWEPT_FACE",FACE,{"disambiguationData":[OSD([subQ16]),TDD([makeQuery(id+"F0.imprint","IMPRINT",EDGE,{"disambiguationData":[TD([[makeQuery(id+"F0.imprint","INTERSECT",VERTEX,{"derivedFrom":[subQ18,subQ16]}),-1.0]])],"derivedFrom":subQ16})])]}),subQ38,makeQuery(id+"F1.opExtrude","SWEPT_FACE",FACE,{"disambiguationData":[OSD([subQ3]),TDD([makeQuery(id+"F0.imprint","IMPRINT",EDGE,{"disambiguationData":[TD([[makeQuery(id+"F0.imprint","INTERSECT",VERTEX,{"derivedFrom":[subQ10,subQ3]}),-1.0]])],"derivedFrom":subQ3})])]}),subQ6,makeQuery(id+"F1.opExtrude","SWEPT_FACE",FACE,{"disambiguationData":[OSD([subQ9]),TDD([makeQuery(id+"F0.imprint","IMPRINT",EDGE,{"disambiguationData":[TD([[subQ36,1.0]])],"derivedFrom":subQ9})])]}),subQ22,subQ32,subQ33,subQ35,subQ20,makeQuery(id+"F3.opExtrude","SWEPT_FACE",FACE,{"disambiguationData":[OSD([sQuery(id+"F2.wireOp",EDGE,"E6.top")])]}),subQ7])],"derivedFrom":subQ19}),makeQuery(id+"F3.boolean.opBoolean","SPLIT",FACE,{"disambiguationData":[TD([subQ19,makeQuery(id+"F1.opExtrude","SWEPT_FACE",FACE,{"disambiguationData":[OSD([subQ15]),TDD([makeQuery(id+"F0.imprint","IMPRINT",EDGE,{"disambiguationData":[TD([[makeQuery(id+"F0.imprint","INTERSECT",VERTEX,{"derivedFrom":[subQ18,subQ15]}),-1.0]])],"derivedFrom":subQ15})])]}),subQ29,makeQuery(id+"F1.opExtrude","SWEPT_FACE",FACE,{"disambiguationData":[OSD([subQ12]),TDD([makeQuery(id+"F0.imprint","IMPRINT",EDGE,{"disambiguationData":[TD([[makeQuery(id+"F0.imprint","INTERSECT",VERTEX,{"derivedFrom":[subQ14,subQ12]}),-1.0]])],"derivedFrom":subQ12})])]}),subQ24,makeQuery(id+"F1.opExtrude","SWEPT_FACE",FACE,{"disambiguationData":[OSD([subQ9]),TDD([makeQuery(id+"F0.imprint","IMPRINT",EDGE,{"disambiguationData":[TD([[subQ30,-1.0]])],"derivedFrom":subQ9})])]}),subQ26,makeQuery(id+"F3.opExtrude","SWEPT_FACE",FACE,{"disambiguationData":[OSD([sQuery(id+"F2.wireOp",EDGE,"E5.bottom")])]}),subQ27,subQ28,subQ32,subQ33,subQ34])],"derivedFrom":subQ19}),makeQuery(id+"F3.boolean.opBoolean","SPLIT",FACE,{"disambiguationData":[TD([subQ19,makeQuery(id+"F1.opExtrude","SWEPT_FACE",FACE,{"disambiguationData":[OSD([subQ13])]}),subQ24,makeQuery(id+"F1.opExtrude","SWEPT_FACE",FACE,{"disambiguationData":[OSD([subQ11,subQ8])]}),subQ26,subQ27,subQ28,makeQuery(id+"F3.opExtrude","SWEPT_FACE",FACE,{"disambiguationData":[OSD([sQuery(id+"F2.wireOp",EDGE,"E5.right")])]})])],"derivedFrom":subQ19}),makeQuery(id+"F3.boolean.opBoolean","SPLIT",FACE,{"disambiguationData":[TD([subQ19,makeQuery(id+"F1.opExtrude","SWEPT_FACE",FACE,{"disambiguationData":[OSD([subQ2])]}),makeQuery(id+"F1.opExtrude","SWEPT_FACE",FACE,{"disambiguationData":[OSD([subQ1,subQ0])]}),subQ6,subQ22,subQ20,subQ7,makeQuery(id+"F3.opExtrude","SWEPT_FACE",FACE,{"disambiguationData":[OSD([sQuery(id+"F2.wireOp",EDGE,"E6.right")])]})])],"derivedFrom":subQ19}),makeQuery(id+"F5.opExtrude","CAP_FACE",FACE,{"disambiguationData":[OSD([sQuery(id+"F4.wireOp",EDGE,"E7.bottom"),sQuery(id+"F4.wireOp",EDGE,"E7.top"),sQuery(id+"F4.wireOp",EDGE,"E7.left"),sQuery(id+"F4.wireOp",EDGE,"E7.right")])],"isStart":true})]});}
            var sketch = newSketch(context, id + "F25", { "sketchPlane" : qUnion([Q0])});
            skCircle(sketch, "E42", {"center": v(-406.4, 139.7) * mm, "radius": 6.35 * mm});
            skCircle(sketch, "E43", {"center": v(0, 139.7) * mm, "radius": 6.35 * mm});
            skCircle(sketch, "E44", {"center": v(406.4, 139.7) * mm, "radius": 6.35 * mm});
            skSolve(sketch);
        }
        {
            var Q0;
            Q0=qSketchRegion(id+"F25",true);
            extrude(context, id + "F26", {"entities" : qUnion([Q0]), "operationType" : NewBodyOperationType.REMOVE, "oppositeDirection" : true, "depth" : 12.7 * mm, "offsetDistance" : 25.4 * mm});
        }
        {
            var Q0;
            {var subQ0=makeQuery(id+"F3.opExtrude","SWEPT_FACE",FACE,{"disambiguationData":[OSD([sQuery(id+"F2.wireOp",EDGE,"E5.left")])]});var subQ2=sQuery(id+"F0.wireOp",EDGE,"E3.right");var subQ3=sQuery(id+"F0.wireOp",EDGE,"E1.right");var subQ4=makeQuery(id+"F1.opExtrude","SWEPT_FACE",FACE,{"disambiguationData":[OSD([subQ3,subQ2])]});var subQ5=sQuery(id+"F0.wireOp",EDGE,"E1.left");var subQ6=sQuery(id+"F0.wireOp",EDGE,"E1.bottom");var subQ7=sQuery(id+"F0.wireOp",EDGE,"E3.bottom");var subQ9=makeQuery(id+"F1.opExtrude","SWEPT_FACE",FACE,{"disambiguationData":[OSD([subQ5]),TDD([makeQuery(id+"F0.imprint","IMPRINT",EDGE,{"disambiguationData":[TD([[makeQuery(id+"F0.imprint","INTERSECT",VERTEX,{"derivedFrom":[subQ6,subQ5]}),-1.0]])],"derivedFrom":subQ5})])]});var subQ10=makeQuery(id+"F1.opExtrude","SWEPT_FACE",FACE,{"disambiguationData":[OSD([subQ6])]});var subQ11=makeQuery(id+"F3.opExtrude","SWEPT_FACE",FACE,{"disambiguationData":[OSD([sQuery(id+"F2.wireOp",EDGE,"E5.right")])]});var subQ17=sQuery(id+"F0.wireOp",EDGE,"E0.right");var subQ18=makeQuery(id+"F1.opExtrude","CAP_FACE",FACE,{"disambiguationData":[OSD([sQuery(id+"F0.wireOp",EDGE,"E0.bottom"),sQuery(id+"F0.wireOp",EDGE,"E0.top"),sQuery(id+"F0.wireOp",EDGE,"E0.left"),subQ17,subQ6,sQuery(id+"F0.wireOp",EDGE,"E1.top"),subQ5,subQ3,sQuery(id+"F0.wireOp",EDGE,"E2.bottom"),sQuery(id+"F0.wireOp",EDGE,"E2.top"),sQuery(id+"F0.wireOp",EDGE,"E2.left"),sQuery(id+"F0.wireOp",EDGE,"E2.right"),subQ7,sQuery(id+"F0.wireOp",EDGE,"E3.top"),sQuery(id+"F0.wireOp",EDGE,"E3.left"),subQ2])],"isStart":false});Q0=makeQuery(id+"F9.boolean.opBoolean","SPLIT",FACE,{"disambiguationData":[TD([subQ10])],"derivedFrom":makeQuery(id+"F3.boolean.opBoolean","SPLIT",FACE,{"disambiguationData":[TD([subQ18,subQ10,subQ9,subQ4,makeQuery(id+"F1.opExtrude","SWEPT_FACE",FACE,{"disambiguationData":[OSD([subQ7]),TDD([makeQuery(id+"F0.imprint","IMPRINT",EDGE,{"disambiguationData":[TD([[makeQuery(id+"F0.imprint","INTERSECT",VERTEX,{"derivedFrom":[subQ17,subQ7]}),-1.0]])],"derivedFrom":subQ7})])]}),makeQuery(id+"F3.opExtrude","SWEPT_FACE",FACE,{"disambiguationData":[OSD([sQuery(id+"F2.wireOp",EDGE,"E5.bottom")])]}),subQ0,subQ11])],"derivedFrom":subQ18})});}
            var sketch = newSketch(context, id + "F27", { "sketchPlane" : qUnion([Q0])});
            skCircle(sketch, "E45", {"center": v(-406.4, -139.7) * mm, "radius": 6.35 * mm});
            skSolve(sketch);
        }
        {
            var Q0;
            Q0=qSketchRegion(id+"F27",true);
            extrude(context, id + "F28", {"entities" : qUnion([Q0]), "operationType" : NewBodyOperationType.REMOVE, "oppositeDirection" : true, "depth" : 12.7 * mm, "offsetDistance" : 25.4 * mm});
        }
        {
            var Q0;
            {var subQ0=makeQuery(id+"F3.opExtrude","SWEPT_FACE",FACE,{"disambiguationData":[OSD([sQuery(id+"F2.wireOp",EDGE,"E6.left")])]});var subQ1=sQuery(id+"F0.wireOp",EDGE,"E2.right");var subQ2=sQuery(id+"F0.wireOp",EDGE,"E2.bottom");var subQ3=sQuery(id+"F0.wireOp",EDGE,"E3.bottom");var subQ5=makeQuery(id+"F1.opExtrude","SWEPT_FACE",FACE,{"disambiguationData":[OSD([subQ1]),TDD([makeQuery(id+"F0.imprint","IMPRINT",EDGE,{"disambiguationData":[TD([[makeQuery(id+"F0.imprint","INTERSECT",VERTEX,{"derivedFrom":[subQ2,subQ1]}),-1.0]])],"derivedFrom":subQ1})])]});var subQ6=sQuery(id+"F0.wireOp",EDGE,"E3.left");var subQ7=sQuery(id+"F0.wireOp",EDGE,"E2.left");var subQ8=makeQuery(id+"F1.opExtrude","SWEPT_FACE",FACE,{"disambiguationData":[OSD([subQ7,subQ6])]});var subQ9=makeQuery(id+"F1.opExtrude","SWEPT_FACE",FACE,{"disambiguationData":[OSD([subQ2])]});var subQ16=makeQuery(id+"F3.opExtrude","SWEPT_FACE",FACE,{"disambiguationData":[OSD([sQuery(id+"F2.wireOp",EDGE,"E6.right")])]});var subQ17=sQuery(id+"F0.wireOp",EDGE,"E0.left");var subQ18=makeQuery(id+"F1.opExtrude","CAP_FACE",FACE,{"disambiguationData":[OSD([sQuery(id+"F0.wireOp",EDGE,"E0.bottom"),sQuery(id+"F0.wireOp",EDGE,"E0.top"),subQ17,sQuery(id+"F0.wireOp",EDGE,"E0.right"),sQuery(id+"F0.wireOp",EDGE,"E1.bottom"),sQuery(id+"F0.wireOp",EDGE,"E1.top"),sQuery(id+"F0.wireOp",EDGE,"E1.left"),sQuery(id+"F0.wireOp",EDGE,"E1.right"),subQ2,sQuery(id+"F0.wireOp",EDGE,"E2.top"),subQ7,subQ1,subQ3,sQuery(id+"F0.wireOp",EDGE,"E3.top"),subQ6,sQuery(id+"F0.wireOp",EDGE,"E3.right")])],"isStart":false});Q0=makeQuery(id+"F7.boolean.opBoolean","SPLIT",FACE,{"disambiguationData":[TD([subQ9])],"derivedFrom":makeQuery(id+"F3.boolean.opBoolean","SPLIT",FACE,{"disambiguationData":[TD([subQ18,subQ9,subQ8,subQ5,makeQuery(id+"F1.opExtrude","SWEPT_FACE",FACE,{"disambiguationData":[OSD([subQ3]),TDD([makeQuery(id+"F0.imprint","IMPRINT",EDGE,{"disambiguationData":[TD([[makeQuery(id+"F0.imprint","INTERSECT",VERTEX,{"derivedFrom":[subQ17,subQ3]}),1.0]])],"derivedFrom":subQ3})])]}),makeQuery(id+"F3.opExtrude","SWEPT_FACE",FACE,{"disambiguationData":[OSD([sQuery(id+"F2.wireOp",EDGE,"E6.top")])]}),subQ0,subQ16])],"derivedFrom":subQ18})});}
            var sketch = newSketch(context, id + "F29", { "sketchPlane" : qUnion([Q0])});
            skCircle(sketch, "E46", {"center": v(406.4, -139.7) * mm, "radius": 6.35 * mm});
            skSolve(sketch);
        }
        {
            var Q0;
            Q0=qSketchRegion(id+"F29",true);
            extrude(context, id + "F30", {"entities" : qUnion([Q0]), "operationType" : NewBodyOperationType.REMOVE, "oppositeDirection" : true, "depth" : 12.7 * mm, "offsetDistance" : 25.4 * mm});
        }
    });
